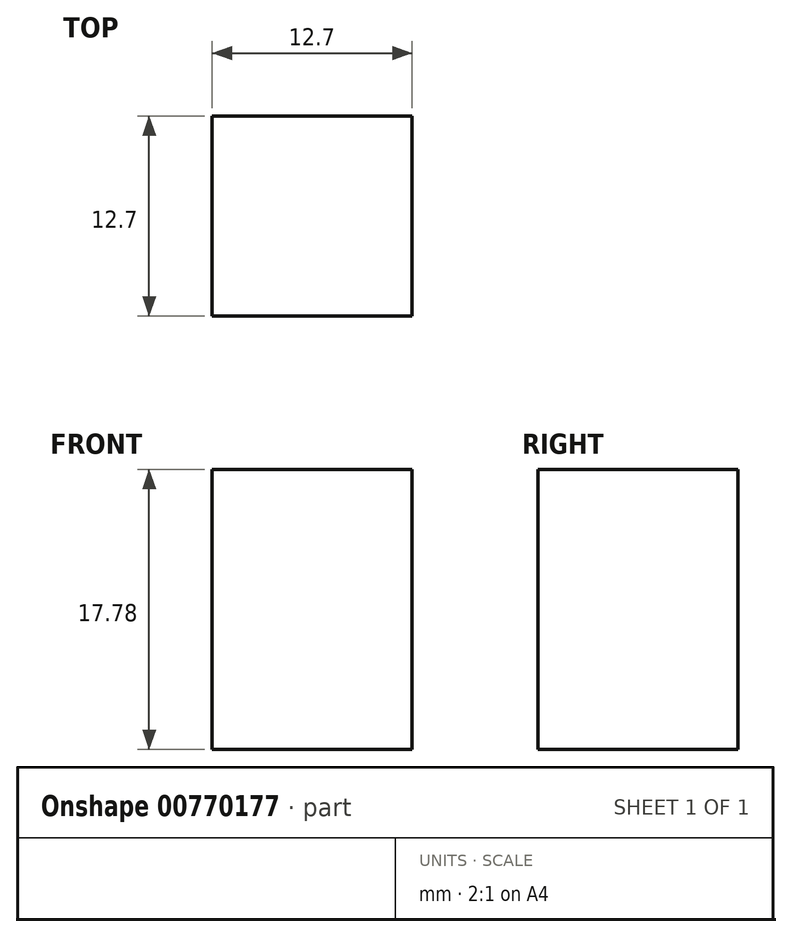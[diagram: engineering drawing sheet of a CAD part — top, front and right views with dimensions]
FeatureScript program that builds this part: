
annotation { "Feature Type Name" : "Feature", "Feature Type Description" : "" }
export const myFeature = defineFeature(function(context is Context, id is Id, definition is map)
    precondition{}
    {
        {
            var Q0;
            Q0=qCreatedBy(makeId("Top.planeOp"),FACE);
            var sketch = newSketch(context, id + "F0", { "sketchPlane" : qUnion([Q0])});
            skLineSegment(sketch, "E0.bottom", {"start": v(-12.7, 36.7) * mm, "end": v(0, 36.7) * mm});
            skLineSegment(sketch, "E0.top", {"start": v(-12.7, 49.4) * mm, "end": v(0, 49.4) * mm});
            skLineSegment(sketch, "E0.left", {"start": v(-12.7, 36.7) * mm, "end": v(-12.7, 49.4) * mm});
            skLineSegment(sketch, "E0.right", {"start": v(0, 36.7) * mm, "end": v(0, 49.4) * mm});
            skSolve(sketch);
        }
        {
            var Q0;
            Q0=qSketchRegion(id+"F0",true);
            extrude(context, id + "F1", {"entities" : qUnion([Q0]), "depth" : 17.78 * mm, "offsetDistance" : 25.4 * mm});
        }
    });
